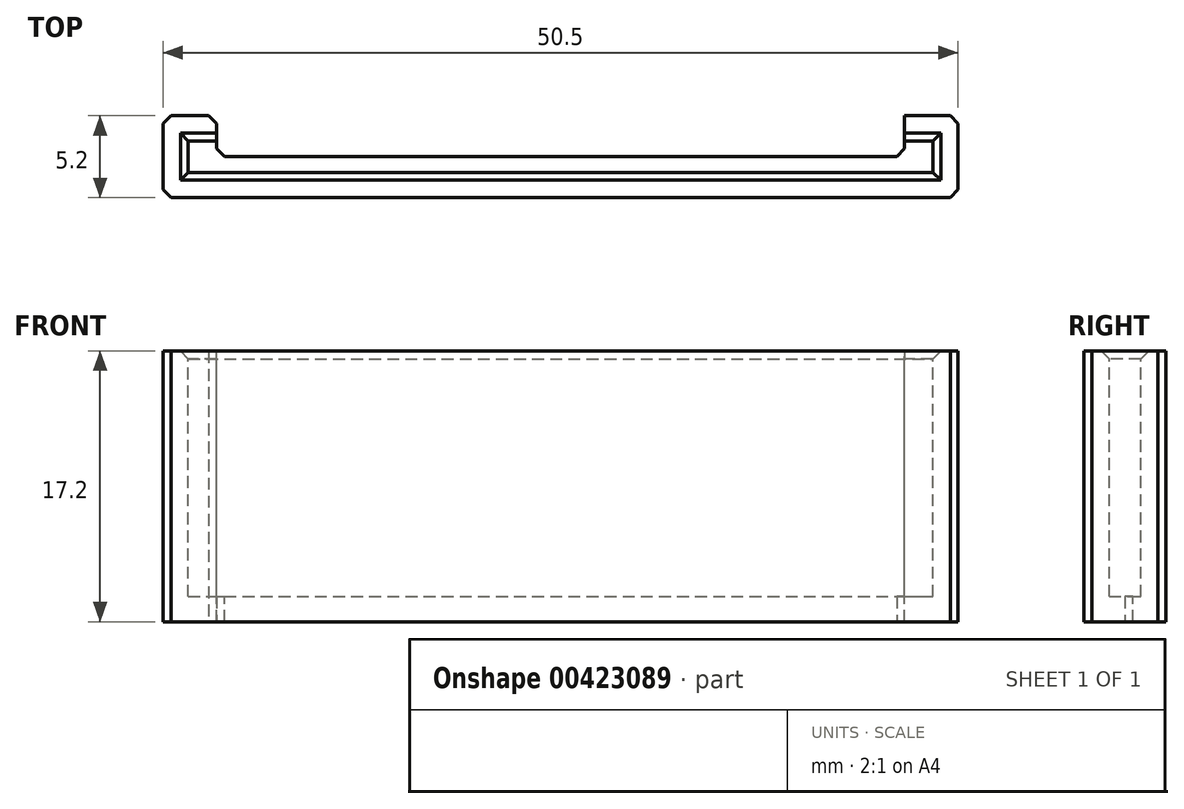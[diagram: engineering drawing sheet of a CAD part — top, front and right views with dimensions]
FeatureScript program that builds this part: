
annotation { "Feature Type Name" : "Feature", "Feature Type Description" : "" }
export const myFeature = defineFeature(function(context is Context, id is Id, definition is map)
    precondition{}
    {
        {
            var Q0;
            Q0=qCreatedBy(makeId("Top.planeOp"),FACE);
            var sketch = newSketch(context, id + "F0", { "sketchPlane" : qUnion([Q0])});
            skLineSegment(sketch, "E0.bottom", {"start": v(0, 0) * mm, "end": v(47.3, 0) * mm});
            skLineSegment(sketch, "E0.top", {"start": v(0, 2) * mm, "end": v(47.3, 2) * mm});
            skLineSegment(sketch, "E0.left", {"start": v(0, 0) * mm, "end": v(0, 2) * mm});
            skLineSegment(sketch, "E0.right", {"start": v(47.3, 0) * mm, "end": v(47.3, 2) * mm});
            skSolve(sketch);
        }
        {
            var Q0;
            Q0=makeQuery(id+"F0.imprint","IMPRINT",FACE,{"disambiguationData":[TD([[makeQuery(id+"F0.imprint","IMPRINT",EDGE,{"derivedFrom":sQuery(id+"F0.wireOp",EDGE,"E0.bottom")}),1.0]])]});
            extrude(context, id + "F1", {"entities" : qUnion([Q0]), "oppositeDirection" : true, "depth" : 15.6 * mm, "offsetDistance" : 25 * mm});
        }
        {
            var Q0;
            Q0=makeQuery(id+"F1.opExtrude","CAP_FACE",FACE,{"disambiguationData":[OSD([sQuery(id+"F0.wireOp",EDGE,"E0.bottom"),sQuery(id+"F0.wireOp",EDGE,"E0.top"),sQuery(id+"F0.wireOp",EDGE,"E0.left"),sQuery(id+"F0.wireOp",EDGE,"E0.right")])],"isStart":true});
            shell(context, id + "F2", {"entities" : qUnion([Q0]), "thickness" : 1.6 * mm, "oppositeDirection" : true});
        }
        {
            var Q0;
            Q0=makeQuery(id+"F1.opExtrude","CAP_FACE",FACE,{"disambiguationData":[OSD([sQuery(id+"F0.wireOp",EDGE,"E0.bottom"),sQuery(id+"F0.wireOp",EDGE,"E0.top"),sQuery(id+"F0.wireOp",EDGE,"E0.left"),sQuery(id+"F0.wireOp",EDGE,"E0.right")])],"isStart":true});
            var sketch = newSketch(context, id + "F3", { "sketchPlane" : qUnion([Q0])});
            skLineSegment(sketch, "E1", {"start": v(23.65, -1.6) * mm, "end": v(23.65, 3.6) * mm, "construction": true});
            skLineSegment(sketch, "E2.bottom", {"start": v(1.8, 3.6) * mm, "end": v(45.5, 3.6) * mm});
            skLineSegment(sketch, "E2.top", {"start": v(1.8, 2) * mm, "end": v(45.5, 2) * mm});
            skLineSegment(sketch, "E2.left", {"start": v(1.8, 3.6) * mm, "end": v(1.8, 2) * mm});
            skLineSegment(sketch, "E2.right", {"start": v(45.5, 3.6) * mm, "end": v(45.5, 2) * mm});
            skSolve(sketch);
        }
        {
            var Q0;
            Q0=makeQuery(id+"F3.imprint","IMPRINT",FACE,{"disambiguationData":[TD([[makeQuery(id+"F3.imprint","IMPRINT",EDGE,{"derivedFrom":sQuery(id+"F3.wireOp",EDGE,"E2.bottom")}),-1.0]])]});
            var Q1;
            Q1=makeQuery(id+"F1.opExtrude","CAP_FACE",FACE,{"disambiguationData":[OSD([sQuery(id+"F0.wireOp",EDGE,"E0.bottom"),sQuery(id+"F0.wireOp",EDGE,"E0.top"),sQuery(id+"F0.wireOp",EDGE,"E0.left"),sQuery(id+"F0.wireOp",EDGE,"E0.right")])],"isStart":false});
            extrude(context, id + "F4", {"entities" : qUnion([Q0]), "operationType" : NewBodyOperationType.REMOVE, "endBound" : BoundingType.UP_TO_SURFACE, "oppositeDirection" : true, "depth" : 13 * mm, "endBoundEntityFace" : qUnion([Q1]), "offsetDistance" : 25 * mm});
        }
        {
            var Q0;
            {var subQ0=sQuery(id+"F0.wireOp",EDGE,"E0.left");var subQ1=sQuery(id+"F0.wireOp",EDGE,"E0.top");Q0=makeQuery(id+"F4.boolean.opBoolean","SPLIT",EDGE,{"disambiguationData":[TD([makeQuery(id+"F2.opShell","OFFSET_FACE",FACE,{"disambiguationData":[OSD([subQ0])]})])],"derivedFrom":makeQuery(id+"F2.opShell","OFFSET_EDGE",EDGE,{"disambiguationData":[OSD([subQ1]),TDD([makeQuery(id+"F1.opExtrude","CAP_EDGE",EDGE,{"disambiguationData":[OSD([subQ1])],"isStart":true})])]})});}
            var Q1;
            Q1=makeQuery(id+"F4.boolean.opBoolean","COPY",EDGE,{"derivedFrom":makeQuery(id+"F4.opExtrude","CAP_EDGE",EDGE,{"disambiguationData":[OSD([sQuery(id+"F3.wireOp",EDGE,"E2.left")])],"isStart":true})});
            var Q2;
            {var subQ0=sQuery(id+"F0.wireOp",EDGE,"E0.right");var subQ1=sQuery(id+"F0.wireOp",EDGE,"E0.top");Q2=makeQuery(id+"F4.boolean.opBoolean","SPLIT",EDGE,{"disambiguationData":[TD([makeQuery(id+"F2.opShell","OFFSET_FACE",FACE,{"disambiguationData":[OSD([subQ0])]})])],"derivedFrom":makeQuery(id+"F2.opShell","OFFSET_EDGE",EDGE,{"disambiguationData":[OSD([subQ1]),TDD([makeQuery(id+"F1.opExtrude","CAP_EDGE",EDGE,{"disambiguationData":[OSD([subQ1])],"isStart":true})])]})});}
            var Q3;
            Q3=makeQuery(id+"F4.boolean.opBoolean","COPY",EDGE,{"derivedFrom":makeQuery(id+"F4.opExtrude","CAP_EDGE",EDGE,{"disambiguationData":[OSD([sQuery(id+"F3.wireOp",EDGE,"E2.right")])],"isStart":true})});
            var Q4;
            Q4=makeQuery(id+"F1.opExtrude","SWEPT_EDGE",EDGE,{"disambiguationData":[OSD([sQuery(id+"F0.wireOp",EDGE,"E0.top"),sQuery(id+"F0.wireOp",EDGE,"E0.right")])]});
            var Q5;
            Q5=makeQuery(id+"F1.opExtrude","SWEPT_EDGE",EDGE,{"disambiguationData":[OSD([sQuery(id+"F0.wireOp",EDGE,"E0.bottom"),sQuery(id+"F0.wireOp",EDGE,"E0.right")])]});
            var Q6;
            Q6=makeQuery(id+"F1.opExtrude","SWEPT_EDGE",EDGE,{"disambiguationData":[OSD([sQuery(id+"F0.wireOp",EDGE,"E0.top"),sQuery(id+"F0.wireOp",EDGE,"E0.left")])]});
            var Q7;
            Q7=makeQuery(id+"F1.opExtrude","SWEPT_EDGE",EDGE,{"disambiguationData":[OSD([sQuery(id+"F0.wireOp",EDGE,"E0.bottom"),sQuery(id+"F0.wireOp",EDGE,"E0.left")])]});
            var Q8;
            {var subQ0=sQuery(id+"F0.wireOp",EDGE,"E0.bottom");Q8=makeQuery(id+"F2.opShell","OFFSET_EDGE",EDGE,{"disambiguationData":[OSD([subQ0]),TDD([makeQuery(id+"F1.opExtrude","CAP_EDGE",EDGE,{"disambiguationData":[OSD([subQ0])],"isStart":true})])]});}
            var Q9;
            {var subQ0=sQuery(id+"F0.wireOp",EDGE,"E0.left");Q9=makeQuery(id+"F2.opShell","OFFSET_EDGE",EDGE,{"disambiguationData":[OSD([subQ0]),TDD([makeQuery(id+"F1.opExtrude","CAP_EDGE",EDGE,{"disambiguationData":[OSD([subQ0])],"isStart":true})])]});}
            var Q10;
            {var subQ0=sQuery(id+"F0.wireOp",EDGE,"E0.right");Q10=makeQuery(id+"F2.opShell","OFFSET_EDGE",EDGE,{"disambiguationData":[OSD([subQ0]),TDD([makeQuery(id+"F1.opExtrude","CAP_EDGE",EDGE,{"disambiguationData":[OSD([subQ0])],"isStart":true})])]});}
            var Q11;
            Q11=makeQuery(id+"F4.boolean.opBoolean","COPY",EDGE,{"derivedFrom":makeQuery(id+"F4.opExtrude","SWEPT_EDGE",EDGE,{"disambiguationData":[OSD([sQuery(id+"F0.wireOp",EDGE,"E0.top"),sQuery(id+"F3.wireOp",EDGE,"E2.bottom"),sQuery(id+"F3.wireOp",EDGE,"E2.right")])]})});
            var Q12;
            Q12=makeQuery(id+"F4.boolean.opBoolean","COPY",EDGE,{"derivedFrom":makeQuery(id+"F4.opExtrude","SWEPT_EDGE",EDGE,{"disambiguationData":[OSD([sQuery(id+"F0.wireOp",EDGE,"E0.top"),sQuery(id+"F3.wireOp",EDGE,"E2.bottom"),sQuery(id+"F3.wireOp",EDGE,"E2.left")])]})});
            chamfer(context, id + "F5", {"entities" : qUnion([Q0, Q1, Q2, Q3, Q4, Q5, Q6, Q7, Q8, Q9, Q10, Q11, Q12]), "width" : .5 * mm, "tangentPropagation" : true});
        }
        {
            var Q0;
            Q0=makeQuery(id+"F4.boolean.opBoolean","COPY",FACE,{"derivedFrom":makeQuery(id+"F4.opExtrude","SWEPT_FACE",FACE,{"disambiguationData":[OSD([sQuery(id+"F3.wireOp",EDGE,"E2.top")])]})});
            extrude(context, id + "F6", {"entities" : qUnion([Q0]), "operationType" : NewBodyOperationType.REMOVE, "oppositeDirection" : true, "depth" : 1 * mm, "offsetDistance" : 25 * mm});
        }
        {
            var Q0;
            Q0=makeQuery(id+"F6.boolean.opBoolean","COPY",EDGE,{"derivedFrom":makeQuery(id+"F6.opExtrude","CAP_EDGE",EDGE,{"disambiguationData":[OSD([sQuery(id+"F0.wireOp",EDGE,"E0.top"),sQuery(id+"F3.wireOp",EDGE,"E2.top"),sQuery(id+"F3.wireOp",EDGE,"E2.left")])],"isStart":false})});
            var Q1;
            Q1=makeQuery(id+"F6.boolean.opBoolean","COPY",EDGE,{"derivedFrom":makeQuery(id+"F6.opExtrude","CAP_EDGE",EDGE,{"disambiguationData":[OSD([sQuery(id+"F0.wireOp",EDGE,"E0.top"),sQuery(id+"F3.wireOp",EDGE,"E2.top"),sQuery(id+"F3.wireOp",EDGE,"E2.right")])],"isStart":false})});
            chamfer(context, id + "F7", {"entities" : qUnion([Q0, Q1]), "width" : .5 * mm, "tangentPropagation" : true});
        }
    });
